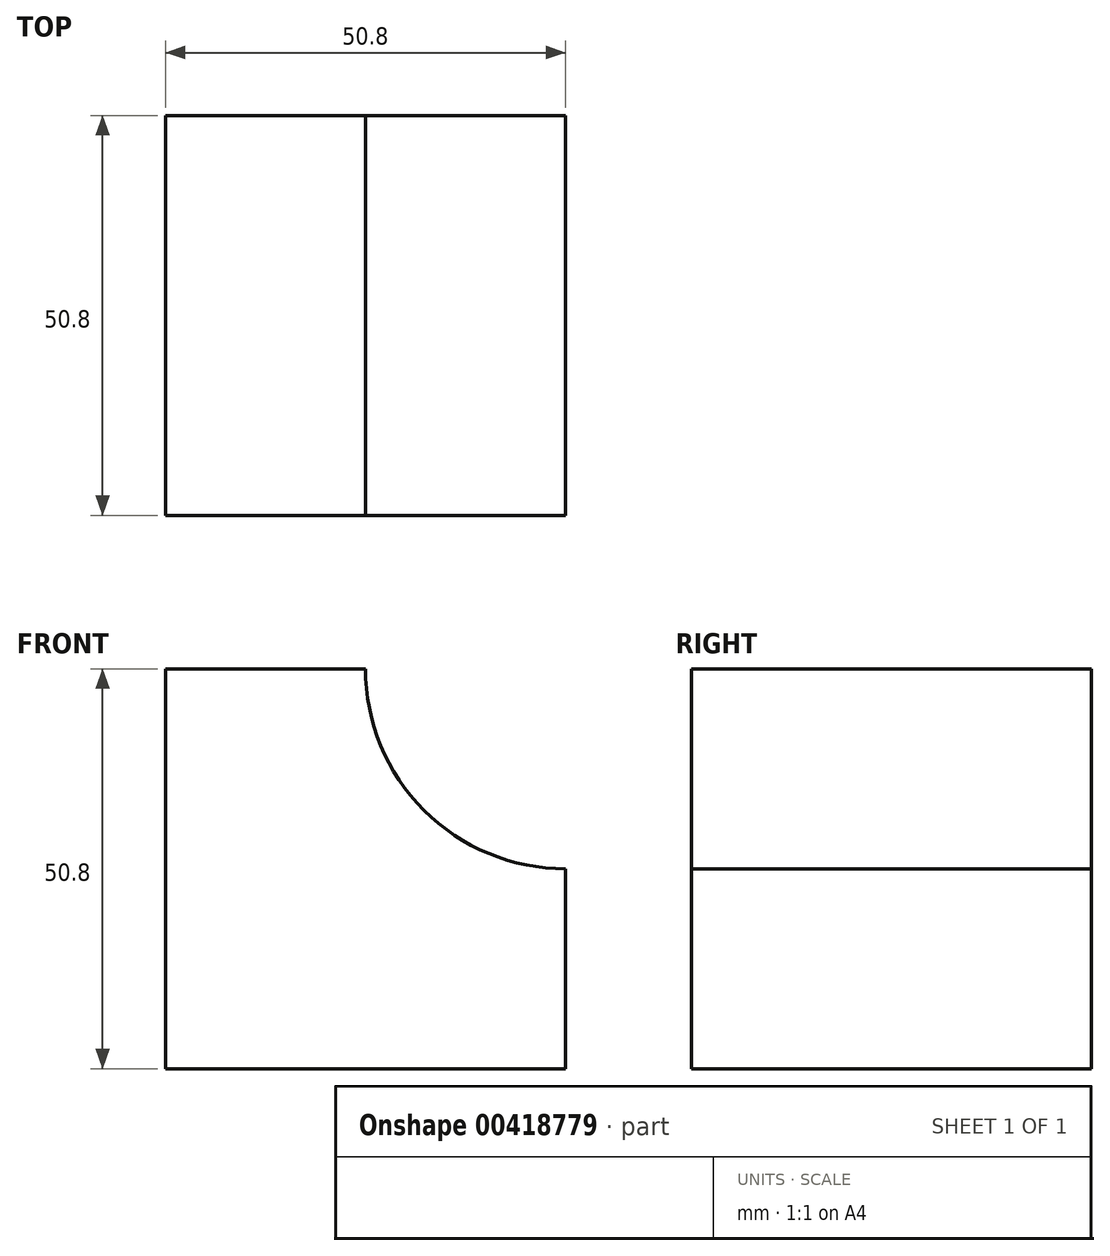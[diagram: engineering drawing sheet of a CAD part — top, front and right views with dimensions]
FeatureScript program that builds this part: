
annotation { "Feature Type Name" : "Feature", "Feature Type Description" : "" }
export const myFeature = defineFeature(function(context is Context, id is Id, definition is map)
    precondition{}
    {
        {
            var Q0;
            Q0=qCreatedBy(makeId("Front.planeOp"),FACE);
            var sketch = newSketch(context, id + "F0", { "sketchPlane" : qUnion([Q0])});
            skLineSegment(sketch, "E0", {"start": v(0, 0) * mm, "end": v(-50.8, 0) * mm});
            skLineSegment(sketch, "E1", {"start": v(-50.8, 0) * mm, "end": v(-50.8, 50.8) * mm});
            skLineSegment(sketch, "E2", {"start": v(-50.8, 50.8) * mm, "end": v(0, 50.8) * mm});
            skLineSegment(sketch, "E3", {"start": v(0, 50.8) * mm, "end": v(0, 0) * mm});
            skArc(sketch, "E4", {"start": v(-25.4, 50.8) * mm, "mid": v(-17.97, 32.83) * mm, "end": v(0, 25.4) * mm});
            skLineSegment(sketch, "E5", {"start": v(-25.4, 50.8) * mm, "end": v(0, 50.8) * mm});
            skLineSegment(sketch, "E6", {"start": v(0, 25.4) * mm, "end": v(0, 50.8) * mm});
            skSolve(sketch);
        }
        {
            var Q0;
            Q0 = qSketchRegion(id + "F0", true);
            extrude(context, id + "F1", {"entities" : qUnion([Q0]), "depth" : 50.8 * mm});
        }
        {
            var Q0;
            Q0=makeQuery(id+"F1.opExtrude","CAP_FACE",FACE,{"disambiguationData":[OSD([sQuery(id+"F0.wireOp",EDGE,"E0"),sQuery(id+"F0.wireOp",EDGE,"E1"),sQuery(id+"F0.wireOp",EDGE,"E2"),sQuery(id+"F0.wireOp",EDGE,"E3"),sQuery(id+"F0.wireOp",EDGE,"E5"),sQuery(id+"F0.wireOp",EDGE,"E6")])],"isStart":false});
            var sketch = newSketch(context, id + "F2", { "sketchPlane" : qUnion([Q0])});
            skArc(sketch, "E7", {"start": v(-25.4, 50.8) * mm, "mid": v(-17.98, 32.82) * mm, "end": v(0, 25.4) * mm});
            skLineSegment(sketch, "E8", {"start": v(0, 50.8) * mm, "end": v(0, 25.4) * mm});
            skLineSegment(sketch, "E9", {"start": v(-25.4, 50.8) * mm, "end": v(0, 50.8) * mm});
            skSolve(sketch);
        }
        {
            var Q0;
            Q0 = qSketchRegion(id + "F2", true);
            extrude(context, id + "F3", {"entities" : qUnion([Q0]), "operationType" : NewBodyOperationType.REMOVE, "oppositeDirection" : true, "depth" : 50.8 * mm});
        }
    });
